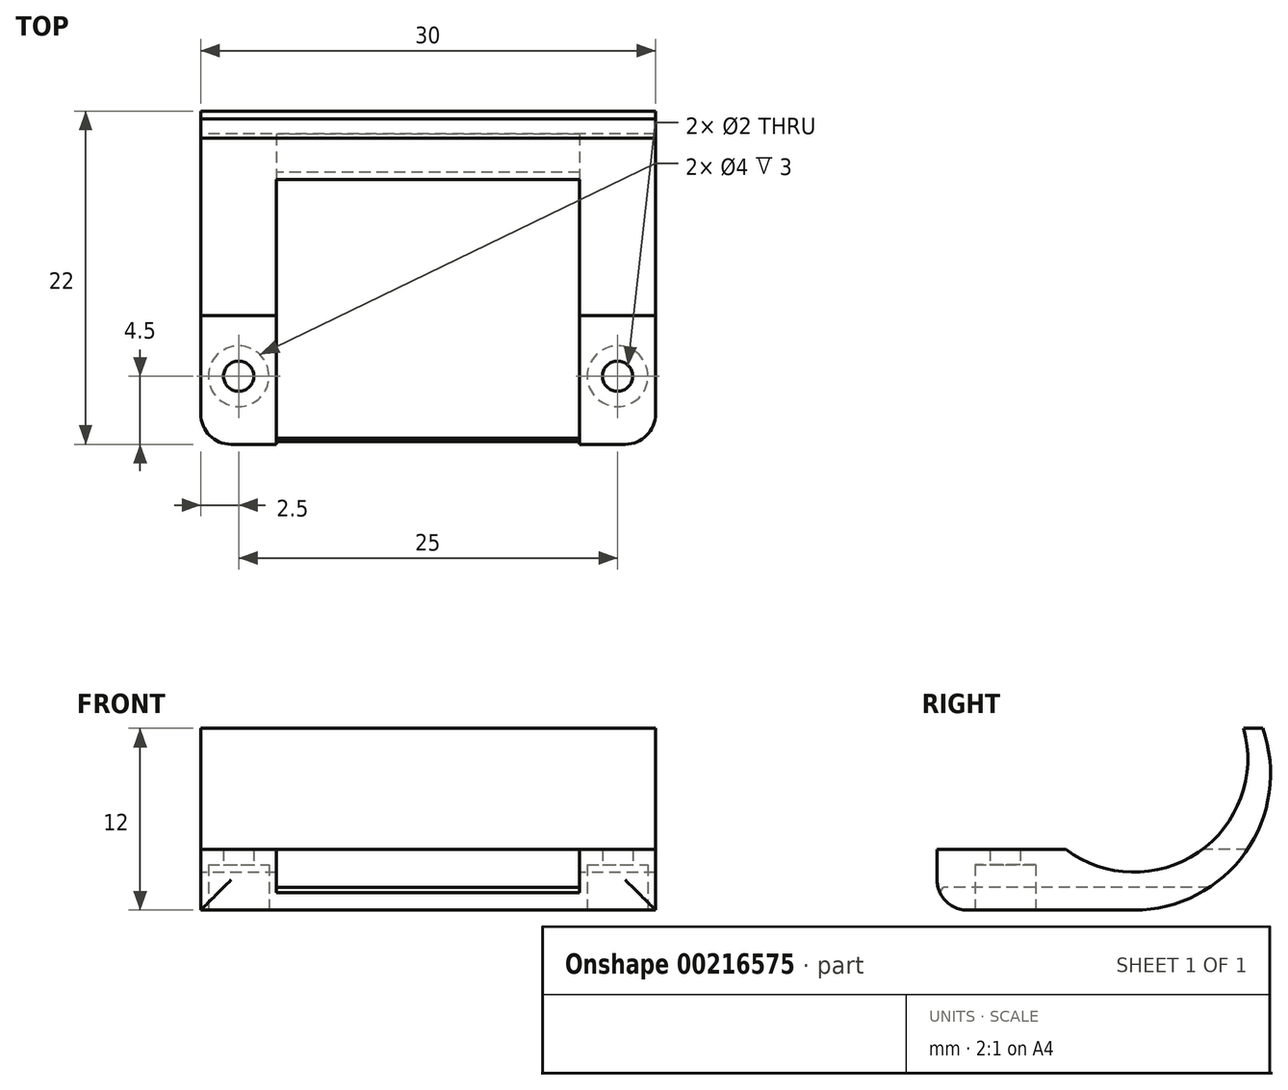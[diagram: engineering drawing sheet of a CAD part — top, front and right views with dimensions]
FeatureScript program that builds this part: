
annotation { "Feature Type Name" : "Feature", "Feature Type Description" : "" }
export const myFeature = defineFeature(function(context is Context, id is Id, definition is map)
    precondition{}
    {
        {
            var Q0;
            Q0=qCreatedBy(makeId("Top.planeOp"),FACE);
            var sketch = newSketch(context, id + "F0", { "sketchPlane" : qUnion([Q0])});
            skLineSegment(sketch, "E0.bottom", {"start": v(-15, 11) * mm, "end": v(15, 11) * mm});
            skLineSegment(sketch, "E0.top", {"start": v(-15, -11) * mm, "end": v(15, -11) * mm});
            skLineSegment(sketch, "E0.left", {"start": v(-15, 11) * mm, "end": v(-15, -11) * mm});
            skLineSegment(sketch, "E0.right", {"start": v(15, 11) * mm, "end": v(15, -11) * mm});
            skSolve(sketch);
        }
        {
            var Q0;
            Q0 = qSketchRegion(id + "F0", true);
            extrude(context, id + "F1", {"entities" : qUnion([Q0]), "depth" : 12 * mm});
        }
        {
            var Q0;
            Q0=makeQuery(id+"F1.opExtrude","SWEPT_FACE",FACE,{"disambiguationData":[OSD([sQuery(id+"F0.wireOp",EDGE,"E0.left")])]});
            var sketch = newSketch(context, id + "F2", { "sketchPlane" : qUnion([Q0])});
            skCircle(sketch, "E1", {"center": v(-2, 10) * mm, "radius": 7.5 * mm});
            skLineSegment(sketch, "E2.bottom", {"start": v(-2, 4) * mm, "end": v(15.65, 4) * mm});
            skLineSegment(sketch, "E2.top", {"start": v(-2, 18.68) * mm, "end": v(15.65, 18.68) * mm});
            skLineSegment(sketch, "E2.left", {"start": v(-2, 4) * mm, "end": v(-2, 18.68) * mm});
            skLineSegment(sketch, "E2.right", {"start": v(15.65, 4) * mm, "end": v(15.65, 18.68) * mm});
            skSolve(sketch);
        }
        {
            var Q0;
            Q0 = qSketchRegion(id + "F2", true);
            extrude(context, id + "F3", {"entities" : qUnion([Q0]), "operationType" : NewBodyOperationType.REMOVE, "endBound" : BoundingType.THROUGH_ALL, "oppositeDirection" : true, "depth" : 25 * mm, "hasSecondDirection" : true, "secondDirectionOppositeDirection" : false, "secondDirectionDepth" : 25 * mm});
        }
        {
            var Q0;
            Q0=qCreatedBy(makeId("Right.planeOp"),FACE);
            var sketch = newSketch(context, id + "F4", { "sketchPlane" : qUnion([Q0])});
            skCircle(sketch, "E3", {"center": v(2, 9) * mm, "radius": 9 * mm});
            skLineSegment(sketch, "E4.bottom", {"start": v(2, -9.05) * mm, "end": v(-24.23, -9.05) * mm});
            skLineSegment(sketch, "E4.top", {"start": v(2, 22.43) * mm, "end": v(-24.23, 22.43) * mm});
            skLineSegment(sketch, "E4.left", {"start": v(2, -9.05) * mm, "end": v(2, 22.43) * mm});
            skLineSegment(sketch, "E4.right", {"start": v(-24.23, -9.05) * mm, "end": v(-24.23, 22.43) * mm});
            skSolve(sketch);
        }
        {
            var Q0;
            Q0 = qSketchRegion(id + "F4", true);
            extrude(context, id + "F5", {"entities" : qUnion([Q0]), "operationType" : NewBodyOperationType.INTERSECT, "endBound" : BoundingType.THROUGH_ALL, "depth" : 25 * mm, "hasSecondDirection" : true, "secondDirectionOppositeDirection" : true, "secondDirectionDepth" : 25 * mm});
        }
        {
            var Q0;
            Q0=makeQuery(id+"F1.opExtrude","CAP_EDGE",EDGE,{"disambiguationData":[OSD([sQuery(id+"F0.wireOp",EDGE,"E0.top")])],"isStart":true});
            var Q1;
            Q1=makeQuery(id+"F1.opExtrude","SWEPT_EDGE",EDGE,{"disambiguationData":[OSD([sQuery(id+"F0.wireOp",EDGE,"E0.top"),sQuery(id+"F0.wireOp",EDGE,"E0.left")])]});
            var Q2;
            Q2=makeQuery(id+"F1.opExtrude","SWEPT_EDGE",EDGE,{"disambiguationData":[OSD([sQuery(id+"F0.wireOp",EDGE,"E0.top"),sQuery(id+"F0.wireOp",EDGE,"E0.right")])]});
            fillet(context, id + "F6", {"entities" : qUnion([Q0, Q1, Q2]), "radius" : 2 * mm, "tangentPropagation" : true, "allowEdgeOverflow" : false});
        }
        {
            var Q0;
            Q0=makeQuery(id+"F3.boolean.opBoolean","COPY",FACE,{"derivedFrom":makeQuery(id+"F3.opExtrude","SWEPT_FACE",FACE,{"disambiguationData":[OSD([sQuery(id+"F2.wireOp",EDGE,"E2.bottom")])]})});
            var sketch = newSketch(context, id + "F7", { "sketchPlane" : qUnion([Q0])});
            skLineSegment(sketch, "E5.bottom", {"start": v(-10, 16.1) * mm, "end": v(10, 16.1) * mm});
            skLineSegment(sketch, "E5.top", {"start": v(-10, -18.28) * mm, "end": v(10, -18.28) * mm});
            skLineSegment(sketch, "E5.left", {"start": v(-10, 16.1) * mm, "end": v(-10, -18.28) * mm});
            skLineSegment(sketch, "E5.right", {"start": v(10, 16.1) * mm, "end": v(10, -18.28) * mm});
            skSolve(sketch);
        }
        {
            var Q0;
            Q0 = qSketchRegion(id + "F7", true);
            extrude(context, id + "F8", {"entities" : qUnion([Q0]), "operationType" : NewBodyOperationType.REMOVE, "oppositeDirection" : true, "depth" : 2.5 * mm});
        }
        {
            var Q0;
            Q0=makeQuery(id+"F8.boolean.opBoolean","INTERSECT",EDGE,{"derivedFrom":[makeQuery(id+"F6.opFillet","BLEND_FACE",FACE,{"disambiguationData":[OSD([sQuery(id+"F0.wireOp",EDGE,"E0.top")])]}),makeQuery(id+"F8.opExtrude","CAP_FACE",FACE,{"disambiguationData":[OSD([sQuery(id+"F7.wireOp",EDGE,"E5.bottom"),sQuery(id+"F7.wireOp",EDGE,"E5.top"),sQuery(id+"F7.wireOp",EDGE,"E5.left"),sQuery(id+"F7.wireOp",EDGE,"E5.right")])],"isStart":false})]});
            chamfer(context, id + "F9", {"entities" : qUnion([Q0]), "width" : 0.25 * mm, "tangentPropagation" : true});
        }
        {
            var Q0;
            Q0=makeQuery(id+"F1.opExtrude","CAP_FACE",FACE,{"disambiguationData":[OSD([sQuery(id+"F0.wireOp",EDGE,"E0.bottom"),sQuery(id+"F0.wireOp",EDGE,"E0.top"),sQuery(id+"F0.wireOp",EDGE,"E0.left"),sQuery(id+"F0.wireOp",EDGE,"E0.right")])],"isStart":true});
            var sketch = newSketch(context, id + "F10", { "sketchPlane" : qUnion([Q0])});
            skPoint(sketch, "E6", {"position": v(12.5, 6.5) * mm});
            skPoint(sketch, "E7", {"position": v(-12.5, 6.5) * mm});
            skSolve(sketch);
        }
        {
            var Q0;
            Q0=sQuery(id+"F10.wireOp",VERTEX,"E6");
            var Q1;
            Q1=sQuery(id+"F10.wireOp",VERTEX,"E7");
            var Q2;
            Q2=makeQuery(id+"F1.opExtrude","SWEPT_BODY",BODY,{"disambiguationData":[OSD([sQuery(id+"F0.wireOp",EDGE,"E0.bottom"),sQuery(id+"F0.wireOp",EDGE,"E0.top"),sQuery(id+"F0.wireOp",EDGE,"E0.left"),sQuery(id+"F0.wireOp",EDGE,"E0.right")])]});
            hole(context, id + "F11", {"style" : HoleStyle.C_BORE, "endStyle" : HoleEndStyle.BLIND, "holeDiameter" : 2 * mm, "cBoreDiameter" : 4 * mm, "cBoreDepth" : 3 * mm, "holeDepth" : 8 * mm, "locations" : qUnion([Q0, Q1]), "scope" : qUnion([Q2])});
        }
    });
